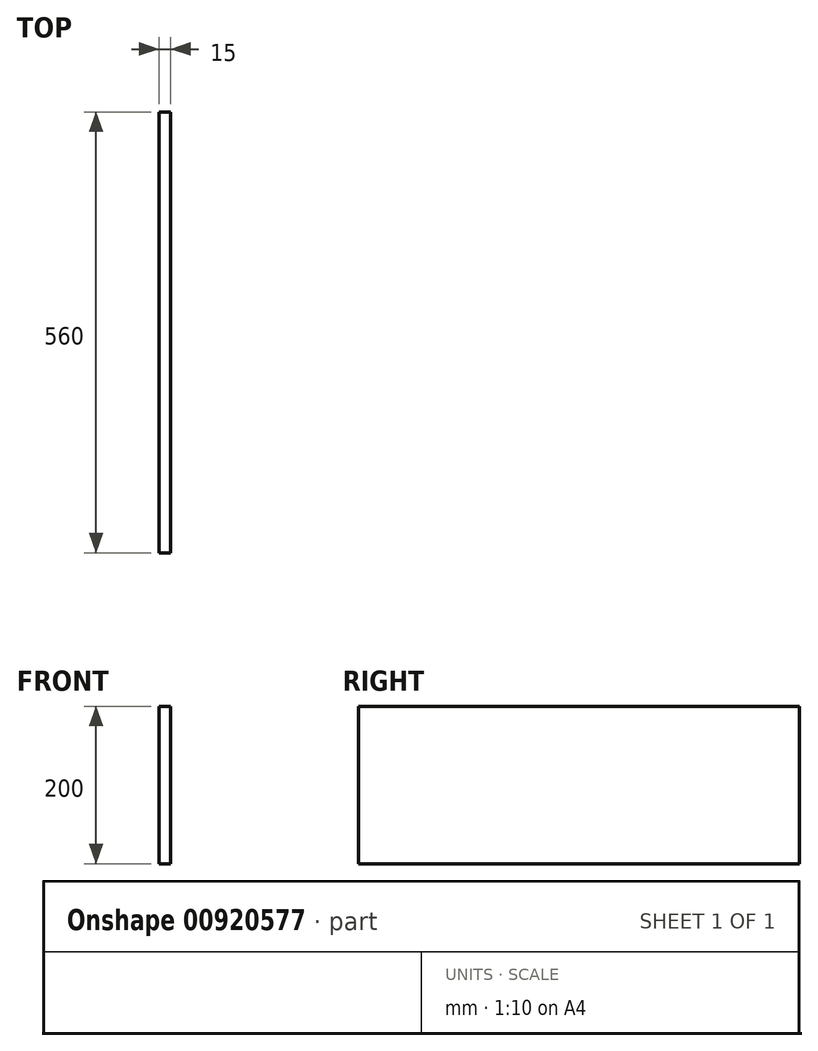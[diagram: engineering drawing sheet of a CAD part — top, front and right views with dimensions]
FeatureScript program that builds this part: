
annotation { "Feature Type Name" : "Feature", "Feature Type Description" : "" }
export const myFeature = defineFeature(function(context is Context, id is Id, definition is map)
    precondition{}
    {
        {
            var Q0;
            Q0=qCreatedBy(makeId("Right.planeOp"),FACE);
            var sketch = newSketch(context, id + "F0", { "sketchPlane" : qUnion([Q0])});
            skLineSegment(sketch, "E0.bottom", {"start": v(280, -100) * mm, "end": v(-280, -100) * mm});
            skLineSegment(sketch, "E0.top", {"start": v(280, 100) * mm, "end": v(-280, 100) * mm});
            skLineSegment(sketch, "E0.left", {"start": v(280, -100) * mm, "end": v(280, 100) * mm});
            skLineSegment(sketch, "E0.right", {"start": v(-280, -100) * mm, "end": v(-280, 100) * mm});
            skPoint(sketch, "E0.middle", {"position": v(0, 0) * mm});
            skSolve(sketch);
        }
        {
            var Q0;
            Q0=qSketchRegion(id+"F0",true);
            extrude(context, id + "F1", {"entities" : qUnion([Q0]), "depth" : 15 * mm, "symmetric" : true});
        }
    });
